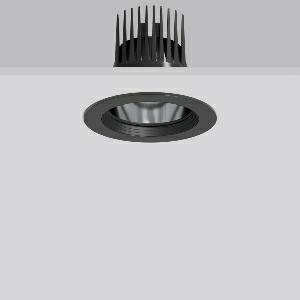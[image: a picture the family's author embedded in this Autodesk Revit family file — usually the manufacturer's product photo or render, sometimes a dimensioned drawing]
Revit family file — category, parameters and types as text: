
# Revit family: heledon_maxi_e_901757_003_3_76_c4bb
name_source: partatom
category: Lighting Fixtures
units: mm (PartAtom-declared; Revit-internal decimal feet)

## family parameters
Cut with Voids When Loaded = No
Host = Face
Light Source = No
Part Type = Normal
Room Calculation Point = No
Round Connector Dimension = Use Diameter
Shared = No

## types (1)
- HELEDON maxi E (1 x LED Modul 935, 3400 lm, 3500)
    Apparent Load = 25 VA
    Approval mark = CE
    CIE Flux Codes = 100 100 100 100 100
    Color Rendering = 92
    Color Temperature = 3500
    Default Elevation = 1800 mm
    Description = Series: HELEDON maxi
Round recessed downlight. Housing: die-cast aluminium, powder-coated. Black plastic ring and recessed LED to prevent glare from the side. Optical assembly with reflector made of MIRO-Silver with 98% total light reflection for outstanding efficiency - can be changed without tools. Best colour rendering index Ra>90. Suitable for Recessed ceiling mounting. Installation without tools thanks to spring fastening system. Including separate LED converter with connecting cable 600 mm.High quality converter without flickering and stroboscopic effect. Through-wiring box (5 pole) available as accessory. The following accessories can be mounted without use of tools: interchangeable lenses, decorative glasses, honeycomb louvre, clear and frosted diffusers, white interchangeable plastic ring. 
Colour: deep black, matt (RAL 9005)
Diameter: 162 mm
Height: 3 mm
Cut-out diameter: 152 mm
Recess height: 200 mm
Luminaire: recess height: 135 mm
Lamp: LED
Socket: without socket
Colour temperature: 3500K
Colour rendering index (CRI): 92
System power: 25 W
Rated luminous flux: 3400 lm
Luminous efficiency: 136 lm/W
Control gear: Converter, dimmable, DALI
Protection class: II
Type of protection: IP 20
    Height = 0 mm  [stored 0 ft]
    Lamp = 1 x LED Modul 935
    Lamp Light Flux = 3400 lm
    Lamp count = 1
    Length = 162 mm
    Lifetime = 50000 h
    Luminous efficacy = 136 lm/W
    Manufacturer = RZB
    ModVariant = No
    Model = 901757.003.3.76
    Mounting Place = Ceiling
    Mounting Type = Recessed
    Number of Poles = 1
    OnlyDefault = Yes
    Power Factor = 1
    Product Name = HELEDON maxi E
    Product group = Recessed downlights
    ProductGroupID = 402
    Protection Class = Protection class II
    Protection Degree = IP 20
    RLX_Detail_Level = 1
    RLX_Emergency_Light_Flux = 0 lm
    RLX_Emergency_Type = 0
    RLX_Emergency_Type_DB = No
    RlxData = <blob elided: 124877 chars, md5=0a4dcbec>
    Socket = socket
    Standby Power = 0 W
    System Light Flux = 3400 lm
    System Power = 25 W
    Type Comments = Product without accessories
    Type Image = 901662.003.jpg
    URL = http://relux.com
    VarID = ---
    Voltage = 230 V
    Voltage Range = 220-240 V
    Weight = 0.00 kg
    Width = 0 mm  [stored 0 ft]

note: [stored X ft] marks values corroborated as IEEE doubles in the binary element streams (Revit-internal decimal feet)

## geometry (parser evidence)
native form markers: Blend x4, Sweep x11
no freeform markers — native parametric forms only
